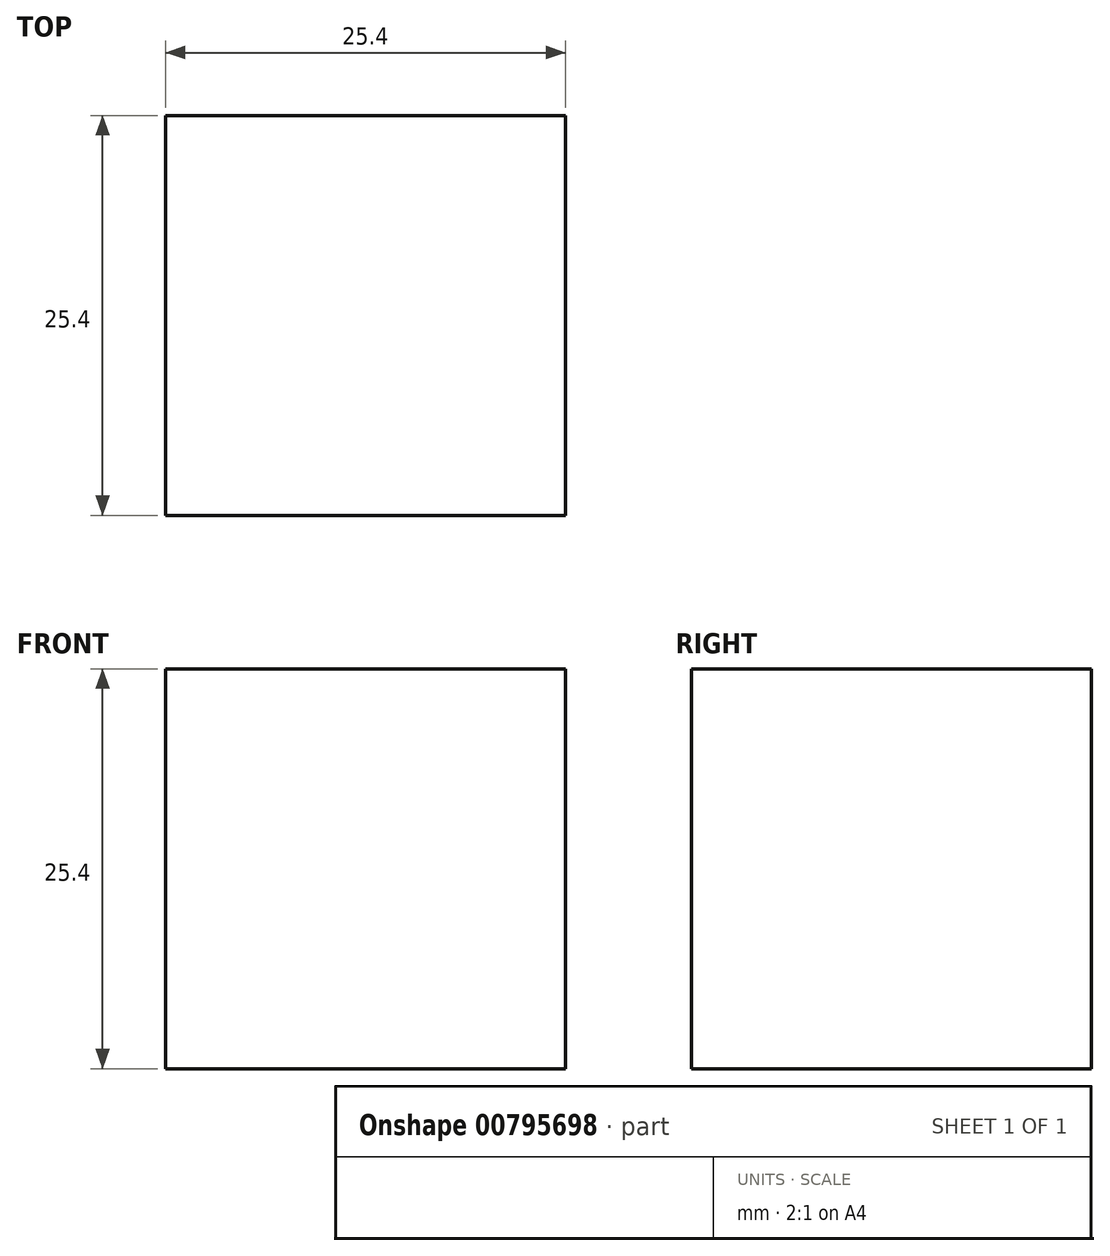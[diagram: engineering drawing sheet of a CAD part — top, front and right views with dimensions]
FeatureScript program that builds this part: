
annotation { "Feature Type Name" : "Feature", "Feature Type Description" : "" }
export const myFeature = defineFeature(function(context is Context, id is Id, definition is map)
    precondition{}
    {
        {
            var Q0;
            Q0=qCreatedBy(makeId("Front.planeOp"),FACE);
            var sketch = newSketch(context, id + "F0", { "sketchPlane" : qUnion([Q0])});
            skLineSegment(sketch, "E0", {"start": v(0, 0) * mm, "end": v(25.4, 0) * mm});
            skSolve(sketch);
        }
        {
            var Q0;
            Q0=sQuery(id+"F0.wireOp",EDGE,"E0");
            extrude(context, id + "F1", {"bodyType" : ToolBodyType.SURFACE, "surfaceEntities" : qUnion([Q0]), "depth" : 25.4 * mm, "offsetDistance" : 25.4 * mm});
        }
        {
            var Q0;
            Q0=makeQuery(id+"F1.opExtrude","SWEPT_FACE",FACE,{"disambiguationData":[OSD([sQuery(id+"F0.wireOp",EDGE,"E0")])]});
            extrude(context, id + "F2", {"entities" : qUnion([Q0]), "oppositeDirection" : true, "depth" : 25.4 * mm, "offsetDistance" : 25.4 * mm});
        }
    });
